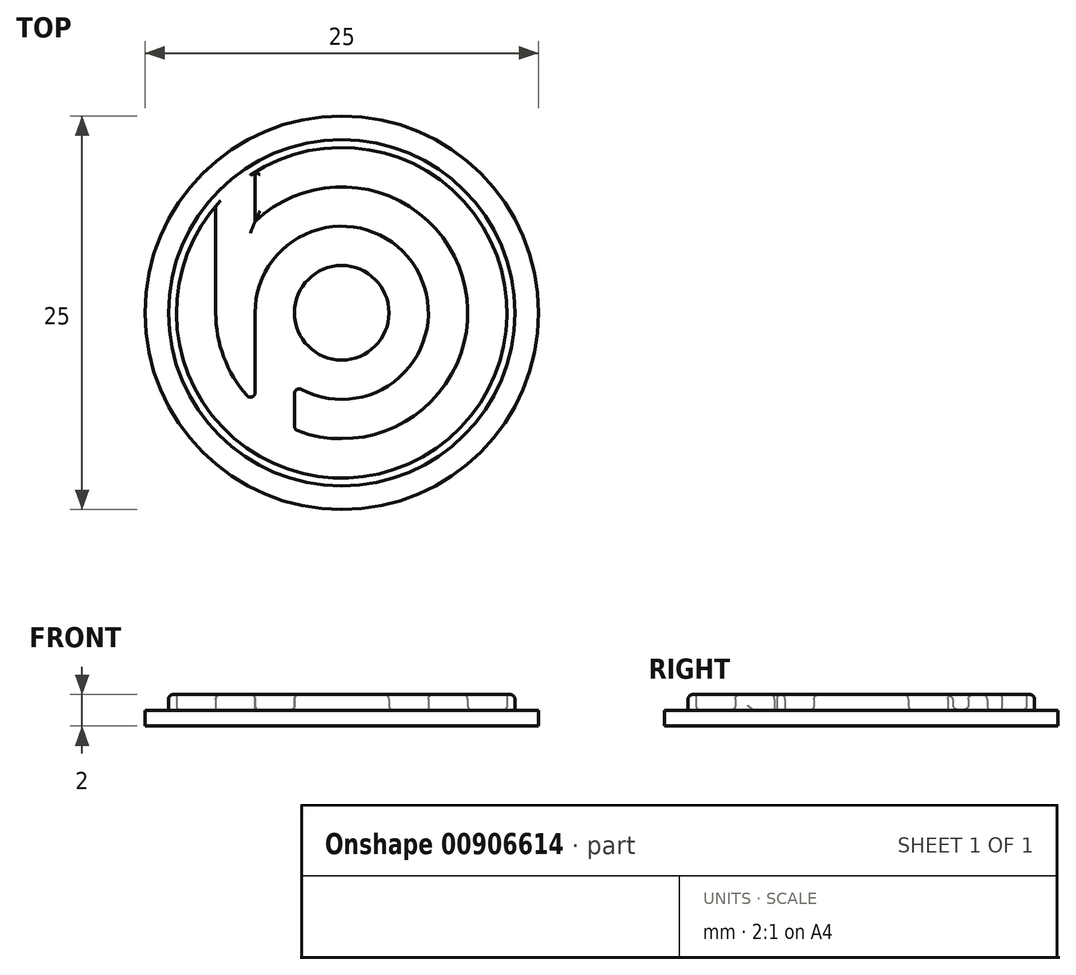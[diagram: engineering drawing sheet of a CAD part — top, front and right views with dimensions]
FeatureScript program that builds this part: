
annotation { "Feature Type Name" : "Feature", "Feature Type Description" : "" }
export const myFeature = defineFeature(function(context is Context, id is Id, definition is map)
    precondition{}
    {
        {
            var Q0;
            Q0=qCreatedBy(makeId("Top.planeOp"),FACE);
            var sketch = newSketch(context, id + "F0", { "sketchPlane" : qUnion([Q0])});
            skCircle(sketch, "E0", {"center": v(-30.21, 41.75) * mm, "radius": 3 * mm});
            skArc(sketch, "E1", {"start": v(-33.21, 37.14) * mm, "mid": v(-25.38, 44.37) * mm, "end": v(-35.71, 41.75) * mm});
            skArc(sketch, "E2", {"start": v(-38.21, 41.75) * mm, "mid": v(-37.56, 38.58) * mm, "end": v(-35.71, 35.94) * mm});
            skArc(sketch, "E3", {"start": v(-38.21, 48.55) * mm, "mid": v(-23.38, 33.77) * mm, "end": v(-35.71, 50.69) * mm});
            skCircle(sketch, "E4", {"center": v(-30.21, 41.75) * mm, "radius": 11 * mm});
            skCircle(sketch, "E5", {"center": v(-30.21, 41.75) * mm, "radius": 12.5 * mm});
            skLineSegment(sketch, "E6", {"start": v(-33.21, 37.14) * mm, "end": v(-33.21, 34.33) * mm});
            skLineSegment(sketch, "E7", {"start": v(-35.71, 41.75) * mm, "end": v(-35.71, 35.94) * mm});
            skPoint(sketch, "E8.orphan", {"position": v(-33.21, 41.75) * mm});
            skLineSegment(sketch, "E9", {"start": v(-38.21, 41.75) * mm, "end": v(-38.21, 48.55) * mm});
            skLineSegment(sketch, "E10", {"start": v(-35.71, 47.55) * mm, "end": v(-35.71, 50.69) * mm});
            skArc(sketch, "E11.trimOffspring", {"start": v(-33.21, 34.33) * mm, "mid": v(-22.35, 43.23) * mm, "end": v(-35.71, 47.55) * mm});
            skSolve(sketch);
        }
        {
            var Q0;
            Q0 = qSketchRegion(id + "F0", true);
            var Q1;
            Q1=makeQuery(id+"F0.imprint","IMPRINT",FACE,{"disambiguationData":[TD([[makeQuery(id+"F0.imprint","IMPRINT",EDGE,{"derivedFrom":sQuery(id+"F0.wireOp",EDGE,"E0")}),-1.0]])]});
            var Q2;
            Q2=makeQuery(id+"F0.imprint","IMPRINT",FACE,{"disambiguationData":[TD([[makeQuery(id+"F0.imprint","IMPRINT",EDGE,{"derivedFrom":sQuery(id+"F0.wireOp",EDGE,"E1")}),-1.0]])]});
            var Q3;
            Q3=makeQuery(id+"F0.imprint","IMPRINT",FACE,{"disambiguationData":[TD([[makeQuery(id+"F0.imprint","IMPRINT",EDGE,{"derivedFrom":sQuery(id+"F0.wireOp",EDGE,"E0")}),1.0]])]});
            extrude(context, id + "F1", {"entities" : qUnion([Q0, Q1, Q2, Q3]), "oppositeDirection" : true, "depth" : 1 * mm, "offsetDistance" : 25 * mm});
        }
        {
            var Q0;
            Q0=makeQuery(id+"F0.imprint","IMPRINT",FACE,{"disambiguationData":[TD([[makeQuery(id+"F0.imprint","IMPRINT",EDGE,{"derivedFrom":sQuery(id+"F0.wireOp",EDGE,"E0")}),1.0]])]});
            var Q1;
            Q1=makeQuery(id+"F0.imprint","IMPRINT",FACE,{"disambiguationData":[TD([[makeQuery(id+"F0.imprint","IMPRINT",EDGE,{"derivedFrom":sQuery(id+"F0.wireOp",EDGE,"E1")}),-1.0]])]});
            extrude(context, id + "F2", {"entities" : qUnion([Q0, Q1]), "operationType" : NewBodyOperationType.ADD, "depth" : 1 * mm, "offsetDistance" : 25 * mm});
        }
        {
            var Q0;
            Q0=makeQuery(id+"F2.opExtrude","CAP_EDGE",EDGE,{"disambiguationData":[OSD([sQuery(id+"F0.wireOp",EDGE,"E4")])],"isStart":false});
            var Q1;
            Q1=makeQuery(id+"F2.opExtrude","CAP_EDGE",EDGE,{"disambiguationData":[OSD([sQuery(id+"F0.wireOp",EDGE,"E4")])],"isStart":true});
            var Q2;
            Q2=makeQuery(id+"F2.opExtrude","CAP_EDGE",EDGE,{"disambiguationData":[OSD([sQuery(id+"F0.wireOp",EDGE,"E2")])],"isStart":false});
            var Q3;
            Q3=makeQuery(id+"F2.opExtrude","CAP_EDGE",EDGE,{"disambiguationData":[OSD([sQuery(id+"F0.wireOp",EDGE,"E0")])],"isStart":false});
            var Q4;
            Q4=makeQuery(id+"F2.opExtrude","CAP_EDGE",EDGE,{"disambiguationData":[OSD([sQuery(id+"F0.wireOp",EDGE,"E1")])],"isStart":false});
            var Q5;
            Q5=makeQuery(id+"F2.opExtrude","CAP_EDGE",EDGE,{"disambiguationData":[OSD([sQuery(id+"F0.wireOp",EDGE,"E11.trimOffspring")])],"isStart":true});
            var Q6;
            Q6=makeQuery(id+"F2.opExtrude","SWEPT_EDGE",EDGE,{"disambiguationData":[OSD([sQuery(id+"F0.wireOp",EDGE,"E2"),sQuery(id+"F0.wireOp",EDGE,"E7")])]});
            var Q7;
            Q7=makeQuery(id+"F2.opExtrude","SWEPT_EDGE",EDGE,{"disambiguationData":[OSD([sQuery(id+"F0.wireOp",EDGE,"E1"),sQuery(id+"F0.wireOp",EDGE,"E6")])]});
            var Q8;
            Q8=makeQuery(id+"F2.opExtrude","SWEPT_EDGE",EDGE,{"disambiguationData":[OSD([sQuery(id+"F0.wireOp",EDGE,"E6"),sQuery(id+"F0.wireOp",EDGE,"E11.trimOffspring")])]});
            var Q9;
            Q9=makeQuery(id+"F2.opExtrude","CAP_EDGE",EDGE,{"disambiguationData":[OSD([sQuery(id+"F0.wireOp",EDGE,"E11.trimOffspring")])],"isStart":false});
            var Q10;
            Q10=makeQuery(id+"F2.opExtrude","CAP_EDGE",EDGE,{"disambiguationData":[OSD([sQuery(id+"F0.wireOp",EDGE,"E6")])],"isStart":false});
            var Q11;
            Q11=makeQuery(id+"F2.opExtrude","CAP_EDGE",EDGE,{"disambiguationData":[OSD([sQuery(id+"F0.wireOp",EDGE,"E10")])],"isStart":false});
            var Q12;
            Q12=makeQuery(id+"F2.opExtrude","CAP_EDGE",EDGE,{"disambiguationData":[OSD([sQuery(id+"F0.wireOp",EDGE,"E10")])],"isStart":true});
            var Q13;
            Q13=makeQuery(id+"F2.opExtrude","CAP_EDGE",EDGE,{"disambiguationData":[OSD([sQuery(id+"F0.wireOp",EDGE,"E3")])],"isStart":true});
            var Q14;
            Q14=makeQuery(id+"F2.opExtrude","CAP_EDGE",EDGE,{"disambiguationData":[OSD([sQuery(id+"F0.wireOp",EDGE,"E0")])],"isStart":true});
            fillet(context, id + "F3", {"entities" : qUnion([Q0, Q1, Q2, Q3, Q4, Q5, Q6, Q7, Q8, Q9, Q10, Q11, Q12, Q13, Q14]), "radius" : .3 * mm, "tangentPropagation" : true, "allowEdgeOverflow" : false});
        }
    });
